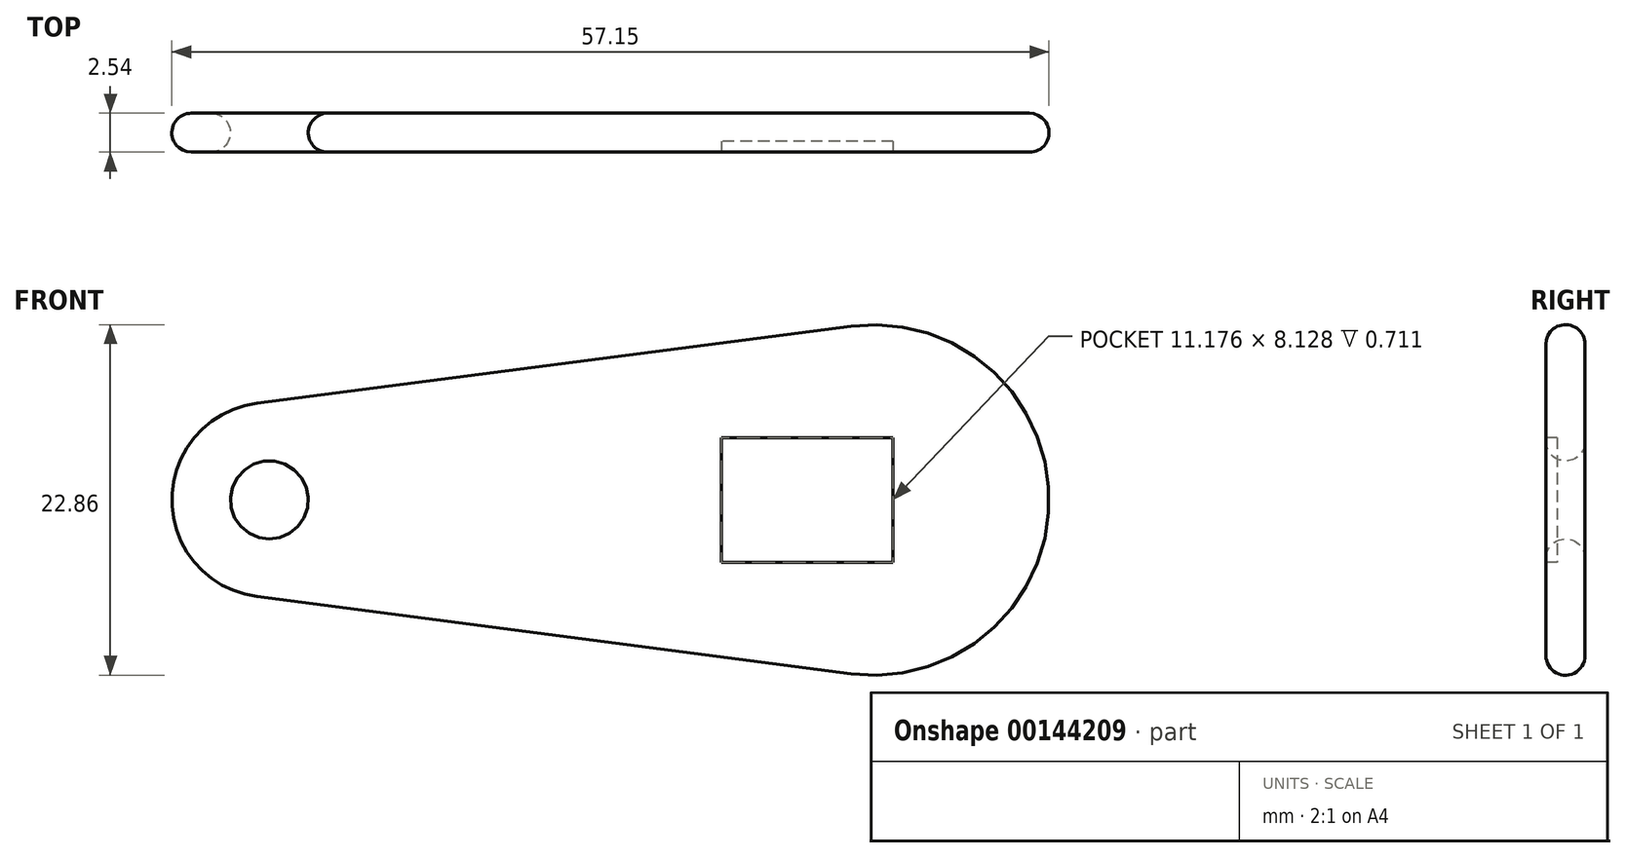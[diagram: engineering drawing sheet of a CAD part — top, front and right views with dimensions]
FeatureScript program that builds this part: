
annotation { "Feature Type Name" : "Feature", "Feature Type Description" : "" }
export const myFeature = defineFeature(function(context is Context, id is Id, definition is map)
    precondition{}
    {
        {
            var Q0;
            Q0=qCreatedBy(makeId("Front.planeOp"),FACE);
            var sketch = newSketch(context, id + "F0", { "sketchPlane" : qUnion([Q0])});
            skPoint(sketch, "E0.middle", {"position": v(0, 0) * mm});
            skCircle(sketch, "E1", {"center": v(-22.86, 0) * mm, "radius": 6.35 * mm});
            skLineSegment(sketch, "E2", {"start": v(-23.68, 6.3) * mm, "end": v(15.04, 11.33) * mm});
            skLineSegment(sketch, "E3", {"start": v(-23.68, -6.3) * mm, "end": v(15.04, -11.33) * mm});
            skCircle(sketch, "E4", {"center": v(16.51, 0) * mm, "radius": 11.43 * mm});
            skLineSegment(sketch, "E5", {"start": v(0, 33.74) * mm, "end": v(0, -77.98) * mm, "construction": true});
            skLineSegment(sketch, "E6", {"start": v(16.51, 11.43) * mm, "end": v(16.51, -11.43) * mm, "construction": true});
            skLineSegment(sketch, "E7", {"start": v(-64.02, 0) * mm, "end": v(74.26, 0) * mm, "construction": true});
            skLineSegment(sketch, "E8", {"start": v(-23.68, 33.1) * mm, "end": v(-23.68, -20.41) * mm, "construction": true});
            skSolve(sketch);
        }
        {
            var Q0;
            Q0=qSketchRegion(id+"F0",true);
            extrude(context, id + "F1", {"entities" : qUnion([Q0]), "endBound" : BoundingType.SYMMETRIC, "depth" : 2.54 * mm});
        }
        {
            var Q0;
            Q0=makeQuery(id+"F1.opExtrude","CAP_FACE",FACE,{"disambiguationData":[OSD([sQuery(id+"F0.wireOp",EDGE,"E1"),sQuery(id+"F0.wireOp",EDGE,"E2"),sQuery(id+"F0.wireOp",EDGE,"E3"),sQuery(id+"F0.wireOp",EDGE,"E4")])],"isStart":false});
            var sketch = newSketch(context, id + "F2", { "sketchPlane" : qUnion([Q0])});
            skCircle(sketch, "E9", {"center": v(-22.86, 0) * mm, "radius": 2.54 * mm});
            skSolve(sketch);
        }
        {
            var Q0;
            Q0=qSketchRegion(id+"F2",true);
            extrude(context, id + "F3", {"entities" : qUnion([Q0]), "operationType" : NewBodyOperationType.REMOVE, "endBound" : BoundingType.SYMMETRIC, "oppositeDirection" : true, "depth" : 50.8 * mm});
        }
        {
            var Q0;
            Q0=makeQuery(id+"F1.opExtrude","CAP_EDGE",EDGE,{"disambiguationData":[OSD([sQuery(id+"F0.wireOp",EDGE,"E2")])],"isStart":false});
            var Q1;
            Q1=makeQuery(id+"F1.opExtrude","CAP_EDGE",EDGE,{"disambiguationData":[OSD([sQuery(id+"F0.wireOp",EDGE,"E2")])],"isStart":true});
            var Q2;
            Q2=makeQuery(id+"F1.opExtrude","CAP_EDGE",EDGE,{"disambiguationData":[OSD([sQuery(id+"F0.wireOp",EDGE,"E4")])],"isStart":false});
            var Q3;
            Q3=makeQuery(id+"F1.opExtrude","SWEPT_FACE",FACE,{"disambiguationData":[OSD([sQuery(id+"F0.wireOp",EDGE,"E4")])]});
            var Q4;
            Q4=makeQuery(id+"F1.opExtrude","CAP_EDGE",EDGE,{"disambiguationData":[OSD([sQuery(id+"F0.wireOp",EDGE,"E1")])],"isStart":false});
            var Q5;
            Q5=makeQuery(id+"F3.boolean.opBoolean","INTERSECT",EDGE,{"derivedFrom":[makeQuery(id+"F1.opExtrude","CAP_FACE",FACE,{"disambiguationData":[OSD([sQuery(id+"F0.wireOp",EDGE,"E1"),sQuery(id+"F0.wireOp",EDGE,"E2"),sQuery(id+"F0.wireOp",EDGE,"E3"),sQuery(id+"F0.wireOp",EDGE,"E4")])],"isStart":true}),makeQuery(id+"F3.opExtrude","SWEPT_FACE",FACE,{"disambiguationData":[OSD([sQuery(id+"F2.wireOp",EDGE,"E9")])]})]});
            var Q6;
            Q6=makeQuery(id+"F3.boolean.opBoolean","INTERSECT",EDGE,{"derivedFrom":[makeQuery(id+"F1.opExtrude","CAP_FACE",FACE,{"disambiguationData":[OSD([sQuery(id+"F0.wireOp",EDGE,"E1"),sQuery(id+"F0.wireOp",EDGE,"E2"),sQuery(id+"F0.wireOp",EDGE,"E3"),sQuery(id+"F0.wireOp",EDGE,"E4")])],"isStart":false}),makeQuery(id+"F3.opExtrude","SWEPT_FACE",FACE,{"disambiguationData":[OSD([sQuery(id+"F2.wireOp",EDGE,"E9")])]})]});
            var Q7;
            Q7=makeQuery(id+"F1.opExtrude","CAP_EDGE",EDGE,{"disambiguationData":[OSD([sQuery(id+"F0.wireOp",EDGE,"E1")])],"isStart":true});
            fillet(context, id + "F4", {"entities" : qUnion([Q0, Q1, Q2, Q3, Q4, Q5, Q6, Q7]), "radius" : 1.27 * mm, "tangentPropagation" : true, "allowEdgeOverflow" : false});
        }
        {
            var Q0;
            Q0=makeQuery(id+"F1.opExtrude","CAP_FACE",FACE,{"disambiguationData":[OSD([sQuery(id+"F0.wireOp",EDGE,"E1"),sQuery(id+"F0.wireOp",EDGE,"E2"),sQuery(id+"F0.wireOp",EDGE,"E3"),sQuery(id+"F0.wireOp",EDGE,"E4")])],"isStart":false});
            var sketch = newSketch(context, id + "F5", { "sketchPlane" : qUnion([Q0])});
            skLineSegment(sketch, "E10.bottom", {"start": v(17.78, 4.06) * mm, "end": v(6.6, 4.06) * mm});
            skLineSegment(sketch, "E10.top", {"start": v(17.78, -4.07) * mm, "end": v(6.6, -4.07) * mm});
            skLineSegment(sketch, "E10.left", {"start": v(17.78, 4.06) * mm, "end": v(17.78, -4.07) * mm});
            skLineSegment(sketch, "E10.right", {"start": v(6.6, 4.06) * mm, "end": v(6.6, -4.07) * mm});
            skSolve(sketch);
        }
        {
            var Q0;
            Q0=qSketchRegion(id+"F5",true);
            extrude(context, id + "F6", {"entities" : qUnion([Q0]), "operationType" : NewBodyOperationType.REMOVE, "oppositeDirection" : true, "depth" : 0.71 * mm});
        }
    });
